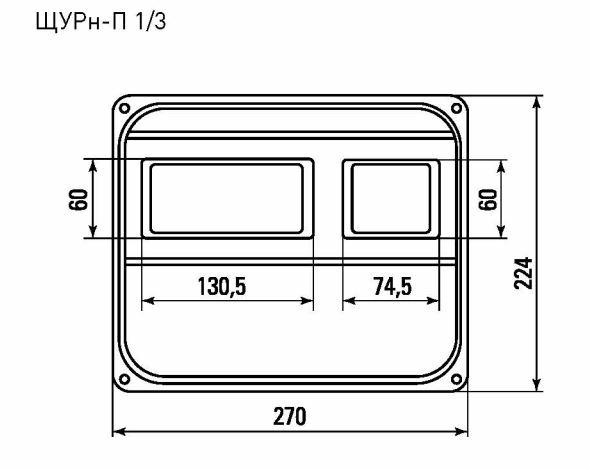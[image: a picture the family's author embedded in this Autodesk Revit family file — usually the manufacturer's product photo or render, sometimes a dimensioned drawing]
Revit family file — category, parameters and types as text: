
# Revit family: EKF_EE_Короб_КСС_Для_УЭРМС(1160х300х160)_Basic
name_source: partatom
category: Электрооборудование
units: mm (PartAtom-declared; Revit-internal decimal feet)

## family parameters
Всегда вертикально = Да
На основе рабочей плоскости = Нет
Общий = Нет
При загрузке вырезать с полостями = Нет
Размер круглого соединителя = Использовать диаметр
Тип детали = Силовой щит
Точка расчета площади = Да

## types (1)
- Короб КСС для УЭРМС (1160х300х160) EKF Basic
    ADSK_Единица измерения = компл.
    ADSK_Завод-изготовитель = EKF
    ADSK_Классификация нагрузок = Прочее
    ADSK_Код изделия = uerms-01kss
    ADSK_Количество = 1
    ADSK_Количество фаз = 3
    ADSK_Коэффициент мощности = 1
    ADSK_Марка = Короб КСС для УЭРМС
    ADSK_Масса = 0
    ADSK_Материал = RAL 7035_Сталь
    ADSK_Наименование = Короб КСС для УЭРМС (1160х300х160) EKF BasicКороб КСС для УЭРМС (1160х300х160) EKF Basic
    ADSK_Напряжение = 400 В
    ADSK_Номинальная мощность = 0 Вт
    ADSK_Обозначение = Короб КСС для УЭРМС
    ADSK_Полная мощность = 0 В·А
    ADSK_Размер_Высота = 1160 мм
    ADSK_Размер_Глубина = 160 мм
    ADSK_Размер_Ширина = 300 мм
    ADSK_Ток = 125 А
    Изготовитель = EKF
    Количество DIN-реек = 0
    Количество модулей на DIN-рейке = 0
    Максимальное количество модулей = 0
    Описание = Короб КСС для УЭРМС (1160х300х160) EKF BasicКороб КСС для УЭРМС (1160х300х160) EKF Basic
    Серия номенклатуры = Basic
    Степень защиты IP = IP31
    ТВ = EKF
    Тип = 217 мм
    Тип установки = Навесной
